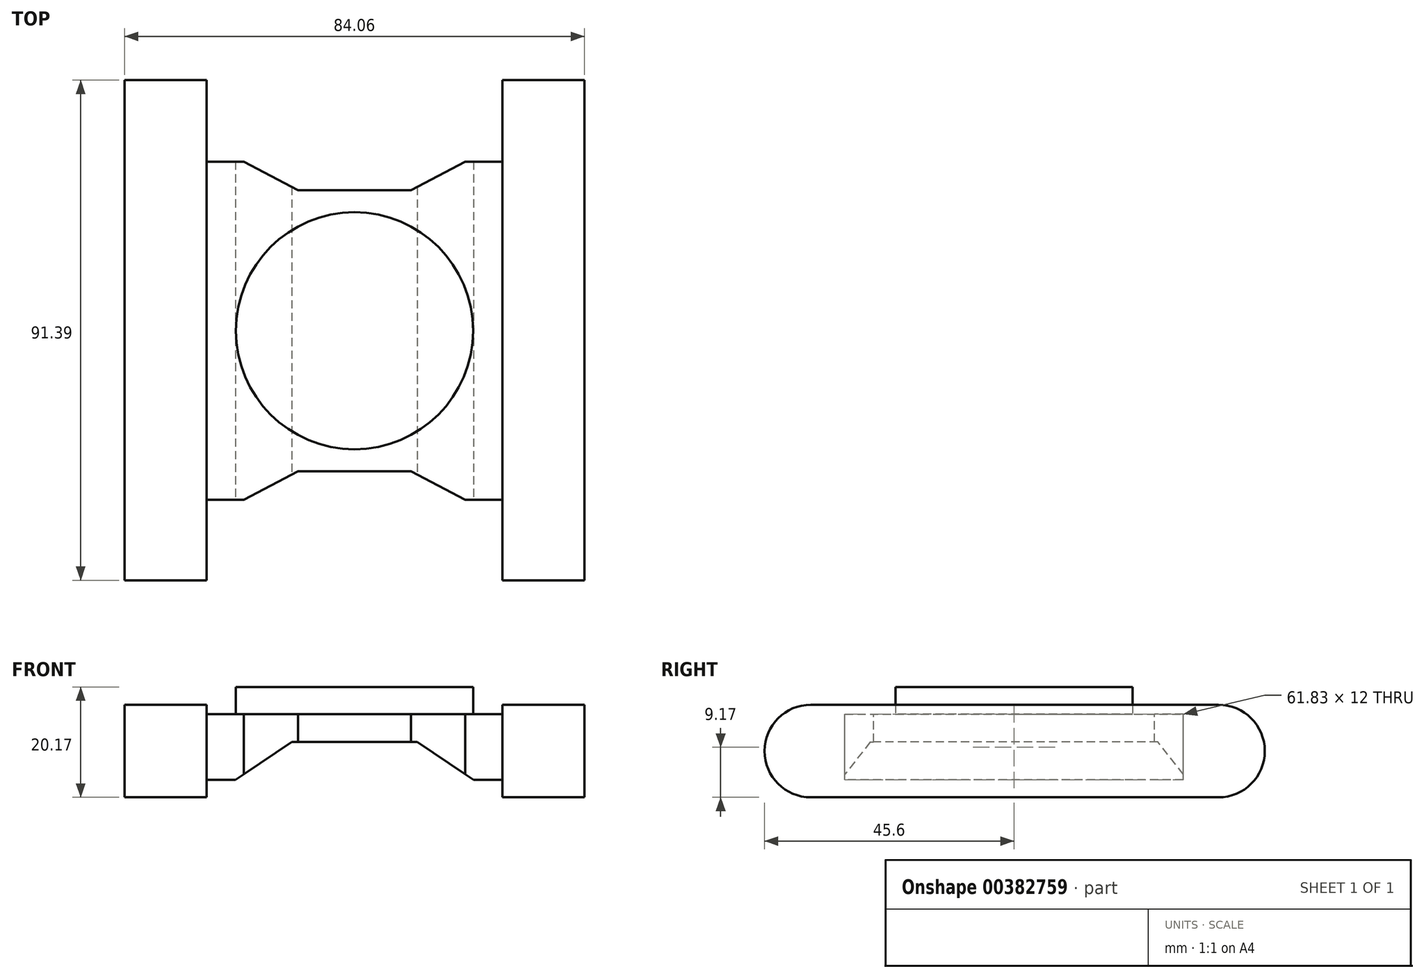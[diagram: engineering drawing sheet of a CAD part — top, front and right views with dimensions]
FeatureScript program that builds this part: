
annotation { "Feature Type Name" : "Feature", "Feature Type Description" : "" }
export const myFeature = defineFeature(function(context is Context, id is Id, definition is map)
    precondition{}
    {
        {
            var Q0;
            Q0=qCreatedBy(makeId("Top.planeOp"),FACE);
            var sketch = newSketch(context, id + "F0", { "sketchPlane" : qUnion([Q0])});
            skCircle(sketch, "E0", {"center": v(0, 0) * mm, "radius": 21.66 * mm});
            skLineSegment(sketch, "E1.left", {"start": v(-27.03, 30.92) * mm, "end": v(-27.03, 0) * mm});
            skLineSegment(sketch, "E2", {"start": v(-27.03, 30.92) * mm, "end": v(-20.22, 30.92) * mm});
            skLineSegment(sketch, "E3", {"start": v(-20.22, 30.92) * mm, "end": v(-10.3, 25.67) * mm});
            skLineSegment(sketch, "E4", {"start": v(-10.3, 25.67) * mm, "end": v(0, 25.67) * mm});
            skLineSegment(sketch, "E5.MirrorCS", {"start": v(-20.22, -30.92) * mm, "end": v(-10.3, -25.67) * mm});
            skLineSegment(sketch, "E6.MirrorCS", {"start": v(-27.03, -30.92) * mm, "end": v(-27.03, 0) * mm});
            skLineSegment(sketch, "E7.MirrorCS", {"start": v(-27.03, -30.92) * mm, "end": v(-20.22, -30.92) * mm});
            skLineSegment(sketch, "E8.MirrorCS", {"start": v(-10.3, -25.67) * mm, "end": v(0, -25.67) * mm});
            skLineSegment(sketch, "E9.MirrorCS", {"start": v(10.3, -25.67) * mm, "end": v(0, -25.67) * mm});
            skLineSegment(sketch, "E10.MirrorCS", {"start": v(27.03, -30.92) * mm, "end": v(20.22, -30.92) * mm});
            skLineSegment(sketch, "E11.MirrorCS", {"start": v(20.22, -30.92) * mm, "end": v(10.3, -25.67) * mm});
            skLineSegment(sketch, "E12.MirrorCS", {"start": v(10.3, 25.67) * mm, "end": v(0, 25.67) * mm});
            skLineSegment(sketch, "E13.MirrorCS", {"start": v(27.03, 30.92) * mm, "end": v(27.03, 0) * mm});
            skLineSegment(sketch, "E14.MirrorCS", {"start": v(20.22, 30.92) * mm, "end": v(10.3, 25.67) * mm});
            skLineSegment(sketch, "E15.MirrorCS", {"start": v(27.03, 30.92) * mm, "end": v(20.22, 30.92) * mm});
            skLineSegment(sketch, "E16.MirrorCS", {"start": v(27.03, -30.92) * mm, "end": v(27.03, 0) * mm});
            skSolve(sketch);
        }
        {
            var Q0;
            Q0=makeQuery(id+"F0.imprint","IMPRINT",FACE,{"disambiguationData":[TD([[makeQuery(id+"F0.imprint","IMPRINT",EDGE,{"derivedFrom":sQuery(id+"F0.wireOp",EDGE,"E0")}),-1.0]])]});
            var Q1;
            Q1=makeQuery(id+"F0.imprint","IMPRINT",FACE,{"disambiguationData":[TD([[makeQuery(id+"F0.imprint","IMPRINT",EDGE,{"derivedFrom":sQuery(id+"F0.wireOp",EDGE,"E0")}),1.0]])]});
            extrude(context, id + "F1", {"entities" : qUnion([Q0, Q1]), "oppositeDirection" : true, "depth" : 12 * mm});
        }
        {
            var Q0;
            Q0=makeQuery(id+"F1.opExtrude","CAP_EDGE",EDGE,{"disambiguationData":[OSD([sQuery(id+"F0.wireOp",EDGE,"E1.left"),sQuery(id+"F0.wireOp",EDGE,"E6.MirrorCS")])],"isStart":false});
            cPoint(context, id + "F2", {"entities" : qUnion([Q0]), "parameter" : 0.5});
        }
        {
            var Q0;
            Q0=makeQuery(id+"F1.opExtrude","SWEPT_FACE",FACE,{"disambiguationData":[OSD([sQuery(id+"F0.wireOp",EDGE,"E1.left"),sQuery(id+"F0.wireOp",EDGE,"E6.MirrorCS")])]});
            var Q1;
            Q1 = qCreatedBy(id + "F2" ,VERTEX);
            cPlane(context, id + "F3", {"entities" : qUnion([Q0, Q1]), "cplaneType" : CPlaneType.PLANE_POINT, "offset" : 25 * mm, "width" : 150 * mm, "height" : 150 * mm});
        }
        {
            var Q0;
            Q0=qCreatedBy(id+"F3.planeOp",FACE);
            var sketch = newSketch(context, id + "F4", { "sketchPlane" : qUnion([Q0])});
            skLineSegment(sketch, "E17.bottom", {"start": v(-37.33, -15.17) * mm, "end": v(37.14, -15.17) * mm});
            skLineSegment(sketch, "E17.top", {"start": v(-37.33, 1.75) * mm, "end": v(37.14, 1.75) * mm});
            skArc(sketch, "E18", {"start": v(-37.33, 1.75) * mm, "mid": v(-45.8, -6.7) * mm, "end": v(-37.33, -15.17) * mm});
            skArc(sketch, "E19", {"start": v(37.14, -15.17) * mm, "mid": v(45.6, -6.7) * mm, "end": v(37.14, 1.75) * mm});
            skSolve(sketch);
        }
        {
            var Q0;
            Q0=makeQuery(id+"F4.imprint","IMPRINT",FACE,{"disambiguationData":[TD([[makeQuery(id+"F4.imprint","IMPRINT",EDGE,{"derivedFrom":sQuery(id+"F4.wireOp",EDGE,"E17.bottom")}),1.0]])]});
            extrude(context, id + "F5", {"entities" : qUnion([Q0]), "depth" : 15 * mm});
        }
        {
            var Q0;
            Q0=makeQuery(id+"F5.opExtrude","SWEPT_BODY",BODY,{"disambiguationData":[OSD([sQuery(id+"F4.wireOp",EDGE,"E17.bottom"),sQuery(id+"F4.wireOp",EDGE,"E17.top"),sQuery(id+"F4.wireOp",EDGE,"E18"),sQuery(id+"F4.wireOp",EDGE,"E19")])]});
            var Q1;
            Q1=qCreatedBy(makeId("Right.planeOp"),FACE);
            mirror(context, id + "F6", {"operationType" : NewBodyOperationType.ADD, "entities" : qUnion([Q0]), "mirrorPlane" : qUnion([Q1])});
        }
        {
            var Q0;
            Q0=qCreatedBy(makeId("Front.planeOp"),FACE);
            var sketch = newSketch(context, id + "F7", { "sketchPlane" : qUnion([Q0])});
            skLineSegment(sketch, "E20", {"start": v(0, -5.06) * mm, "end": v(11.47, -5.06) * mm});
            skLineSegment(sketch, "E21", {"start": v(11.47, -5.06) * mm, "end": v(24.11, -13.61) * mm});
            skLineSegment(sketch, "E22", {"start": v(24.11, -13.61) * mm, "end": v(0, -13.61) * mm});
            skLineSegment(sketch, "E23.MirrorCS", {"start": v(0, -5.06) * mm, "end": v(-11.47, -5.06) * mm});
            skLineSegment(sketch, "E24.MirrorCS", {"start": v(-24.11, -13.61) * mm, "end": v(0, -13.61) * mm});
            skLineSegment(sketch, "E25.MirrorCS", {"start": v(-11.47, -5.06) * mm, "end": v(-24.11, -13.61) * mm});
            skSolve(sketch);
        }
        {
            var Q0;
            Q0 = qSketchRegion(id + "F7", true);
            extrude(context, id + "F8", {"entities" : qUnion([Q0]), "operationType" : NewBodyOperationType.REMOVE, "oppositeDirection" : true, "depth" : 65.8 * mm, "symmetric" : true});
        }
        {
            var Q0;
            Q0=makeQuery(id+"F0.imprint","IMPRINT",FACE,{"disambiguationData":[TD([[makeQuery(id+"F0.imprint","IMPRINT",EDGE,{"derivedFrom":sQuery(id+"F0.wireOp",EDGE,"E0")}),1.0]])]});
            extrude(context, id + "F9", {"entities" : qUnion([Q0]), "operationType" : NewBodyOperationType.ADD, "depth" : 5 * mm});
        }
    });
